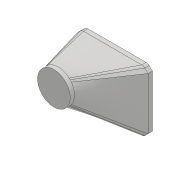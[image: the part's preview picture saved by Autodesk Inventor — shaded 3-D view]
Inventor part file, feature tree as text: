
AUTODESK INVENTOR PART (.ipt)
format: ipt  version: 2018 (Build 220112000, 112)  size: 1,008,640 bytes
history: native  units: mm
features: sketch x44, extrude x38, projected_geometry x36, hole x10, fillet x10, chamfer x10, plane x2, mirror x1, loft x1, other x1
ambient origin geometry x8: Origin, YZ Plane, XZ Plane, XY Plane, X Axis, Y Axis, Z Axis, Center Point
bodies: Solid1 (feature_tree), Solid2 (feature_tree)
feature tree (153):
  extrude  "Extrusion1"  Depth=45.0mm
  extrude  "Extrusion2"  Depth=2.25mm
  hole  "Hole1"  [1 undecoded]
  hole  "Hole2"  [1 undecoded]
  fillet  "Fillet1"  Radius=14.0mm
  extrude  "Extrusion3"  Depth=18.5mm
  extrude  "Extrusion4"  Depth=10.0mm
  extrude  "Extrusion5"  Depth=2.195mm
  extrude  "Extrusion6"  Depth=20.5mm
  hole  "Hole3"  [1 undecoded]
  extrude  "Extrusion7"  Depth=0.5mm
  extrude  "Extrusion8"  Depth=5.0mm TaperAngle=0.0deg
  extrude  "Extrusion9"  Depth=10.0mm
  extrude  "Extrusion10"  Depth=10.0mm
  extrude  "Extrusion11"  Depth=14.5mm
  extrude  "Extrusion12"  Depth=14.5mm
  extrude  "Extrusion13"  Depth=5.0mm
  extrude  "Extrusion14"  Depth=2.25mm
  extrude  "Extrusion15"  Depth=5.0mm
  extrude  "Extrusion16"  Depth=9.0mm
  extrude  "Extrusion17"  Depth=4.0mm
  chamfer  "Chamfer1"  Distance=1.0mm
  fillet  "Fillet7"  Radius=20.7mm
  fillet  "Fillet8"  Radius=32.0mm
  mirror  "Mirror1"
  extrude  "Extrusion19"  Depth=1.0mm TaperAngle=0.0deg
  extrude  "Extrusion20"  Depth=8.0mm
  extrude  "Extrusion21"  Depth=0.2mm TaperAngle=0.0deg
  extrude  "Extrusion22"  Depth=0.5mm TaperAngle=0.0deg
  sketch  "Sketch29"  dims[d77=12.25mm d78=0.0mm d80=8.0mm]
  extrude  "Extrusion23"  Depth=5.0mm TaperAngle=0.0deg
  extrude  "Extrusion24"  Depth=0.2mm TaperAngle=0.0deg
  plane  "Work Plane1"
  extrude  "Extrusion25"  Depth=2.5mm TaperAngle=45.0deg
  extrude  "Extrusion26"  Depth=0.5mm
  extrude  "Extrusion27"  Depth=8.0mm
  extrude  "Extrusion28"  Depth=3.0mm TaperAngle=0.0deg
  extrude  "Extrusion29"  Depth=33.0mm
  extrude  "Extrusion30"  Depth=56.0mm
  extrude  "Extrusion31"  Depth=25.0mm TaperAngle=0.0deg
  chamfer  "Chamfer2"  Distance=6.0mm
  hole  "Hole6"  [1 undecoded]
  chamfer  "Chamfer3"  Distance=40.0mm
  extrude  "Extrusion32"  Depth=12.0mm
  extrude  "Extrusion33"  Depth=40.0mm TaperAngle=0.0deg
  chamfer  "Chamfer4"  Distance=40.0mm
  chamfer  "Chamfer5"  Distance=1.8mm
  chamfer  "Chamfer6"  Distance=3.3mm
  fillet  "Fillet9"  Radius=2.0mm
  extrude  "Extrusion34"  Depth=10.0mm
  chamfer  "Chamfer7"  Distance=1.2mm Angle=45.0deg
  sketch  "Sketch42"  dims[d146=6.0mm d147=0.0mm d149=42.0mm]
  hole  "Hole7"  [1 undecoded]
  hole  "Hole8"  [1 undecoded]
  hole  "Hole9"  [1 undecoded]
  fillet  "Fillet10"  Radius=2.5mm
  chamfer  "Chamfer8"  Distance=3.0mm Angle=45.0deg
  chamfer  "Chamfer9"  Distance=3.0mm Angle=45.0deg
  fillet  "Fillet11"  Radius=3.0mm
  fillet  "Fillet12"  Radius=2.0mm
  extrude  "Extrusion35"  Depth=10.0mm
  sketch  "Sketch45"  dims[d151=4.5mm]
  hole  "Hole10"  [1 undecoded]
  hole  "Hole11"  [1 undecoded]
  hole  "Hole12"  [1 undecoded]
  fillet  "Fillet13"  Radius=2.0mm
  fillet  "Fillet14"  Radius=2.9mm
  fillet  "Fillet15"  Radius=2.9mm
  chamfer  "Chamfer10"  Distance=3.18mm
  extrude  "Extrusion36"  Depth=10.0mm
  sketch  "Sketch47"  dims[d155=28.0mm d156=12.0mm]
  extrude  "Extrusion37"  Depth=10.0mm
  extrude  "Extrusion38"  Depth=10.0mm TaperAngle=45.0deg
  plane  "Work Plane2"
  loft  "Loft1"
  extrude  "Extrusion41"  Depth=10.0mm
  sketch  "Sketch1"  dims[d0=24.5mm d1=45.0mm]
  sketch  "Sketch2"  dims[d2=1.95mm d3=0.0mm d4=2.25mm]
  projected_geometry  "Projected Loop1"
  sketch  "Sketch3"  dims[d5=20.0mm d6=2.25mm]
  projected_geometry  "Projected Loop2"
  sketch  "Sketch4"  dims[d7=5.25mm d8=5.25mm d9=14.0mm]
  projected_geometry  "Projected Loop3"
  sketch  "Sketch5"  dims[d10=5.25mm d11=18.5mm]
  projected_geometry  "Projected Loop4"
  sketch  "Sketch6"  dims[d12=10.0mm d13=0.0mm d14=20.5mm]
  projected_geometry  "Projected Loop5"
  sketch  "Sketch7"  dims[d15=2.0mm d16=2.195mm]
  projected_geometry  "Projected Loop6"
  sketch  "Sketch8"  dims[d17=2.0mm]
  projected_geometry  "Projected Loop7"
  sketch  "Sketch9"  dims[d18=2.4mm d19=6.0mm d20=4.4mm d21=2.0mm d22=90.0deg d23=8.0mm d24=20.594885mm d25=20.5mm]
  projected_geometry  "Projected Loop8"
  projected_geometry  "Projected Loop9"
  sketch  "Sketch10"  dims[d26=26.65mm d27=2.0mm]
  projected_geometry  "Projected Loop10"
  projected_geometry  "Projected Loop11"
  sketch  "Sketch11"  dims[d28=2.0mm]
  projected_geometry  "Projected Loop12"
  sketch  "Sketch12"  dims[d29=2.4mm d30=6.0mm d31=4.4mm d32=2.0mm d33=90.0deg d34=8.0mm d35=20.594885mm d36=0.5mm]
  sketch  "Sketch13"  dims[d37=18.0mm d38=5.0mm d39=0.0mm]
  sketch  "Sketch14"  dims[d41=10.0mm d42=0.0mm d43=24.5mm]
  projected_geometry  "Projected Loop13"
  sketch  "Sketch15"  dims[d44=1.15mm d45=0.0mm d46=10.0mm]
  sketch  "Sketch16"  dims[d47=21.0mm d48=14.5mm]
  projected_geometry  "Projected Loop14"
  sketch  "Sketch17"  dims[d49=20.0mm d50=14.5mm]
  projected_geometry  "Projected Loop15"
  sketch  "Sketch18"  dims[d51=24.5mm d52=5.0mm]
  projected_geometry  "Projected Loop16"
  sketch  "Sketch19"  dims[d53=5.0mm d54=2.25mm]
  projected_geometry  "Projected Loop17"
  sketch  "Sketch20"  dims[d55=2.25mm d56=5.0mm]
  projected_geometry  "Projected Loop18"
  sketch  "Sketch25"  dims[d57=5.0mm d58=9.0mm]
  projected_geometry  "Projected Loop22"
  sketch  "Sketch26"  dims[d59=14.75mm d60=4.0mm d61=1.0mm d62=0.0mm d63=20.7mm]
  sketch  "Sketch27"  dims[d64=2.4mm d65=6.0mm d66=4.4mm d67=2.0mm d68=90.0deg d69=8.0mm d70=20.594885mm d72=32.0mm]
  projected_geometry  "Projected Loop23"
  sketch  "Sketch28"  dims[d73=5.0mm d74=0.0mm d75=1.0mm d76=0.0mm]
  projected_geometry  "Projected Loop24"
  sketch  "Sketch31"  dims[d81=4.5mm d82=0.0mm d84=0.2mm d85=0.0mm]
  projected_geometry  "Projected Loop25"
  sketch  "Sketch32"  dims[d86=21.0mm d87=0.5mm d88=0.0mm]
  projected_geometry  "Projected Loop26"
  sketch  "Sketch33"  dims[d91=8.0mm d92=0.0mm d93=5.0mm d94=0.0mm]
  sketch  "Sketch34"  dims[d95=5.0mm d96=0.0mm d98=0.2mm d99=0.0mm]
  sketch  "Sketch35"  dims[d100=0.2mm d101=0.0mm d102=2.5mm d103=2.0mm d104=45.0deg]
  projected_geometry  "Projected Loop27"
  sketch  "Sketch36"  dims[d105=1.5mm d114=0.5mm]
  sketch  "Sketch37"  dims[d128=4.0mm d129=0.0mm d130=8.0mm]
  sketch  "Sketch38"  dims[d131=3.0mm d132=0.0mm d133=3.0mm d134=0.0mm]
  projected_geometry  "Projected Loop28"
  sketch  "Sketch39"  dims[d135=25.0mm d136=0.0mm d137=33.0mm]
  projected_geometry  "Projected Loop29"
  sketch  "Sketch40"  dims[d138=2.5mm d139=56.0mm]
  projected_geometry  "Projected Loop30"
  sketch  "Sketch41"  dims[d140=25.0mm d141=0.0mm d142=25.0mm d143=0.0mm d144=6.0mm d145=0.0mm]
  sketch  "Sketch44"  dims[d150=4.5mm]
  projected_geometry  "Projected Loop31"
  projected_geometry  "Projected Loop32"
  projected_geometry  "Projected Loop33"
  sketch  "Sketch46"  dims[d152=4.5mm d153=40.0mm d154=0.0mm]
  projected_geometry  "Projected Loop34"
  sketch  "Sketch48"  dims[d157=12.0mm d158=40.0mm d159=0.0mm d160=40.0mm d161=0.0mm]
  projected_geometry  "Projected Loop35"
  sketch  "Sketch49"  dims[d162=20.5mm d163=1.8mm d164=0.0mm]
  other  "Edges1"
  sketch  "Sketch53"  dims[d165=20.5mm d166=3.3mm d167=0.0mm d168=2.0mm d169=2.0mm d170=45.0deg d171=14.0mm d172=3.1mm d173=6.0mm d174=6.3mm d175=2.0mm d176=90.0deg d177=8.0mm d178=20.594885mm d179=1.2mm d180=2.0mm d181=45.0deg d182=7.0mm d183=2.5mm d184=0.0mm d185=7.0mm d186=2.5mm d187=0.0mm d188=3.0mm d189=15.0mm d190=45.0deg d191=3.0mm d192=15.0mm d193=45.0deg d194=3.0mm d195=15.0mm d196=45.0deg d197=2.0mm d198=12.0mm d199=2.0mm d200=15.0mm d201=20.0mm d202=0.0mm d203=2.0mm d204=15.0mm d205=45.0deg d206=2.9mm d207=2.9mm d208=3.18mm d209=3.18mm d210=4.0mm d211=6.0mm d212=6.3mm d213=2.0mm d214=90.0deg d215=8.0mm d216=20.594885mm d217=1.567mm d218=25.0mm d219=6.3mm d220=2.0mm d221=90.0deg d222=25.0mm d223=20.594885mm d224=2.15mm d225=20.0mm d226=4.4mm d227=2.0mm d228=90.0deg d229=10.0mm d230=0.0mm d231=0.5mm d232=2.0mm d233=15.0mm d234=45.0deg d235=2.0mm d236=15.0mm d237=45.0deg d238=1.0mm d239=3.0mm d240=3.9mm d241=3.9mm d242=3.5mm d243=0.0mm d244=2.75mm d245=2.75mm d246=2.5mm d247=1.567mm d248=4.0mm d249=4.4mm d250=2.0mm d251=90.0deg d252=40.0mm d253=20.594885mm d254=2.1mm d255=4.0mm d256=4.4mm d257=2.0mm d258=90.0deg d259=28.25mm d260=0.0mm d261=3.9mm d262=4.0mm d263=4.4mm d264=2.0mm d265=90.0deg d266=20.0mm d267=0.0mm d268=0.2mm d269=2.0mm d270=2.0mm d271=1.8mm d272=15.0mm d273=45.0deg d274=2.0mm d275=0.0mm d276=20.0mm d277=4.2mm d278=0.0mm d279=5.0mm d280=0.0mm d281=25.0mm d282=15.0mm d283=0.0mm d284=90.0deg d285=0.0mm d286=90.0deg d308=2.0mm d309=0.0mm]
  projected_geometry  "Projected Loop39"
  projected_geometry  "Project Cut Edges1"
  projected_geometry  "Project Cut Edges2"
  projected_geometry  "Project Cut Edges3"
note: 10 required parameter values undecoded (feature->parameter linkage not recoverable at this tier; creation-order binding heuristic only, values carry confidence <= 0.55)
